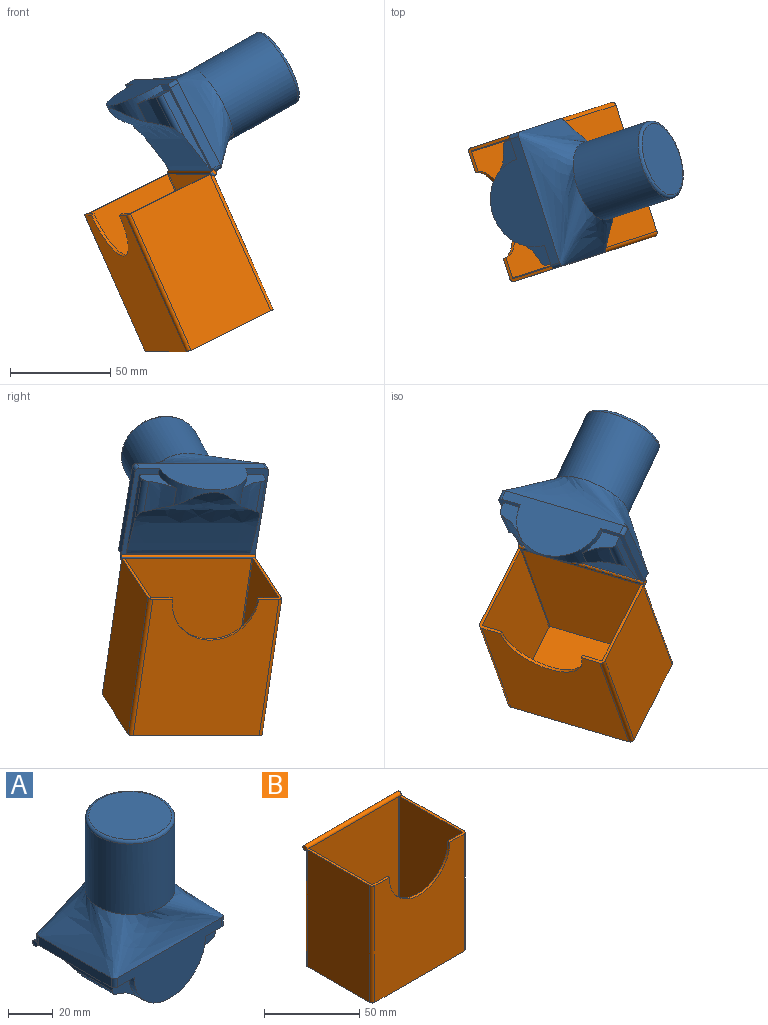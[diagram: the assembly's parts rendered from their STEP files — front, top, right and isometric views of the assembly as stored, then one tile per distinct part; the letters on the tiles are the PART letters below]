
ASSEMBLY  parts=2 mates=1
PART A: 27 faces, bbox 70x51.5x87.5 mm
  f0: plane 70x48.5mm, normal (0,0,-1), area 341mm2, adj f1,f3,f4,f5,f6,f7,f8,f9
  f1: cylinder r=2mm len=5mm, axis (0,0,-1), area 12.3mm2, adj f0,f2,f6,f9,f12
  f2: plane 66x3.5mm, normal (0,1,0), area 231.1mm2, adj f1,f3,f9,f12
  f3: cylinder r=2mm len=5mm, axis (0,0,-1), area 12.3mm2, adj f0,f2,f7,f9,f12
  f4: plane 66x27.5mm, normal (0,-1,0), area 1125.2mm2, adj f0,f5,f8,f12,f13
  f5: cylinder r=2mm len=5mm, axis (0,0,-1), area 15.7mm2, adj f0,f4,f6,f12
  f6: plane 46x5mm, normal (1,0,0), area 230mm2, adj f0,f1,f5,f12
  f7: plane 46x5mm, normal (-1,0,0), area 230mm2, adj f0,f3,f8,f12
  f8: cylinder r=2mm len=5mm, axis (0,0,-1), area 15.7mm2, adj f0,f4,f7,f12
  f9: cylinder r=1.5mm len=70mm, axis (-1,0,0), area 499.4mm2, adj f0,f1,f2,f3,f10,f11
  f10: plane 3x3mm, normal (1,0,0), area 7.1mm2, adj f9
  f11: plane 3x3mm, normal (-1,0,0), area 7.1mm2, adj f9
  f12: bspline ~70x50mm, area 4300.3mm2, adj f1,f2,f3,f4,f5,f6,f7,f8
  f13: cylinder r=22.5mm len=45mm, axis (0,-1,0), area 358.4mm2, adj f0,f4,f15,f18,f19,f20,f21
  f14: plane 64.76x0.03mm, normal (0,1,0), area 1.9mm2, adj f0,f15,f16,f22
  f15: extruded ~64.76x46.59mm, area 2643.7mm2, adj f13,f14,f16,f17,f19,f21,f22,f23
  f16: plane 44.75x4.25mm, normal (1,0,0), area 144.8mm2, adj f0,f14,f15,f17,f18
  f17: cylinder r=3mm len=23.99mm, axis (0,-1,0), area 97mm2, adj f15,f16,f18,f19
  f18: plane 14.83x14.2mm, normal (0,-1,0), area 89.3mm2, adj f0,f13,f16,f17,f19
  f19: extruded ~17.17x11.63mm, area 184.9mm2, adj f13,f15,f17,f18
  f20: plane 15.47x14.65mm, normal (0,-1,0), area 93.3mm2, adj f0,f13,f21,f22,f23
  f21: extruded ~17.17x12.28mm, area 191.7mm2, adj f13,f15,f20,f23
  f22: plane 44.75x4.25mm, normal (-1,0,0), area 144.8mm2, adj f0,f14,f15,f20,f23
  f23: cylinder r=3mm len=23.99mm, axis (0,-1,0), area 97mm2, adj f15,f20,f21,f22
  f24: cylinder r=20mm len=40mm, axis (0,0,-1), area 4838.1mm2, adj f12,f26
  f25: plane 37x37mm, normal (0,0,1), area 1075.2mm2, adj f26
  f26: torus R=18.5mm, axis (0,0,1), area 288mm2, adj f24,f25
PART B: 24 faces, bbox 70x51.5x76.5 mm
  f0: plane 48.48x12.5mm, normal (0,0,1), area 88.5mm2, adj f2,f5,f8,f9,f12,f14,f17,f18
  f1: plane 48.48x12.5mm, normal (0,0,1), area 88.5mm2, adj f4,f7,f8,f10,f11,f15,f16,f17
  f2: cylinder r=2mm len=75mm, axis (0,0,-1), area 232.2mm2, adj f0,f3,f9,f13,f21
  f3: plane 73.49x66mm, normal (0,1,0), area 4850.6mm2, adj f2,f4,f13,f21
  f4: cylinder r=2mm len=75mm, axis (0,0,-1), area 232.2mm2, adj f1,f3,f10,f13,f21
  f5: cylinder r=0.5mm len=73.5mm, axis (0,0,-1), area 57.7mm2, adj f0,f6,f14,f19,f21
  f6: plane 73.25x66mm, normal (0,-1,0), area 4834.4mm2, adj f5,f7,f19,f21
  f7: cylinder r=0.5mm len=73.5mm, axis (0,0,-1), area 57.7mm2, adj f1,f6,f15,f19,f21
  f8: plane 75x66mm, normal (0,-1,0), area 4154.8mm2, adj f0,f1,f11,f12,f13,f20
  f9: plane 75x46mm, normal (1,0,0), area 3450mm2, adj f0,f2,f12,f13
  f10: plane 75x46mm, normal (-1,0,0), area 3450mm2, adj f1,f4,f11,f13
  f11: cylinder r=2mm len=75mm, axis (0,0,-1), area 235.6mm2, adj f1,f8,f10,f13
  f12: cylinder r=2mm len=75mm, axis (0,0,-1), area 235.6mm2, adj f0,f8,f9,f13
  f13: plane 70x50mm, normal (0,0,-1), area 3496.6mm2, adj f2,f3,f4,f8,f9,f10,f11,f12
  f14: plane 73.5x46mm, normal (-1,0,0), area 3381mm2, adj f0,f5,f18,f19
  f15: plane 73.5x46mm, normal (1,0,0), area 3381mm2, adj f1,f7,f16,f19
  f16: cylinder r=0.5mm len=73.5mm, axis (0,0,-1), area 57.7mm2, adj f1,f15,f17,f19
  f17: plane 73.5x66mm, normal (0,1,0), area 4055.8mm2, adj f0,f1,f16,f18,f19,f20
  f18: cylinder r=0.5mm len=73.5mm, axis (0,0,-1), area 57.7mm2, adj f0,f14,f17,f19
  f19: plane 67x47mm, normal (0,0,1), area 3148.8mm2, adj f5,f6,f7,f14,f15,f16,f17,f18
  f20: cylinder r=22.5mm len=45mm, axis (0,-1,0), area 106mm2, adj f0,f1,f8,f17
  f21: cylinder r=1.5mm len=70mm, axis (-1,0,0), area 511.7mm2, adj f0,f1,f2,f3,f4,f5,f6,f7
  f22: plane 3x3mm, normal (1,0,0), area 7.1mm2, adj f21
  f23: plane 3x3mm, normal (-1,0,0), area 7.1mm2, adj f21
PLACE A rot(axis=(-0.58,0.42,-0.7),92.1deg) t=(-70.67,11.9,97.91)mm
PLACE B rot(axis=(0.29,-0.21,-0.94),75.7deg) t=(-61.15,14.98,-35.25)mm fixed
MATE revolute A.f9 <-> B.f21  axis (0.31,-0.95,0) through (-26.56,-47.39,53.87)mm
